# Revit family: LeL Tago 5.1
name_source: partatom
category: Lighting Fixtures
units: mm (PartAtom-declared; Revit-internal decimal feet)

## family parameters
Cut with Voids When Loaded = Yes
Host = Face
Light Source = No
Part Type = Normal
Room Calculation Point = No
Round Connector Dimension = Use Diameter
Shared = No

## types (6) — shared parameters
Accessories = WCTG21A0F outer casing
CCT = 4000 K
CRI = 80
Default Elevation = 1219 mm
Description = Outdoor Linear Profile
Finish = LeL Black
IK = IK09
IP = IP65 IP67 IP69
Lamp = LED
Lenght = 529 mm  [stored 1.73556 ft]
Manufacturer = L&L Luce&Light
Model = TG51
Outercasing = 529 mm  [stored 1.73556 ft]
URL = https://www.lucelight.it

## per-type parameters (varying)
| type | Alimentazione | Apparent Load | Optic | Rated Power supply | Wattage | Weight |
| 5.1 L 52° 24W 48Vdc | 48 V | 24 VA | TAGO Light source : 5.1 L 52° 24W 48Vdc | 48 V | 24 W | 3.00 kg |
| 5.1 M 30° 24W 48Vdc | 48 V | 24 VA | TAGO Light source : 5.1 M 30° 24W 48Vdc | 48 V | 24 W | 3.00 kg |
| 5.1 S 24° 24W 48Vdc | 48 V | 24 VA | TAGO Light source : 5.1 S 24° 24W 48Vdc | 48 V | 24 W | 3.00 kg |
| 5.1 L 52° 29W 230Vac | 230 V | 29 VA | TAGO Light source : 5.1 L 52° 29W 230Vac | 230 V | 29 W | 3.20 kg |
| 5.1 M 30° 29W 230Vac | 230 V | 29 VA | TAGO Light source : 5.1 M 30° 29W 230Vac | 230 V | 29 W | 3.20 kg |
| 5.1 S 24° 29W 230Vac | 230 V | 29 VA | TAGO Light source : 5.1 S 24° 29W 230Vac | 230 V | 29 W | 3.20 kg |

note: [stored X ft] marks values corroborated as IEEE doubles in the binary element streams (Revit-internal decimal feet)

## geometry (parser evidence)
native form markers: Sweep x3
no freeform markers — native parametric forms only
